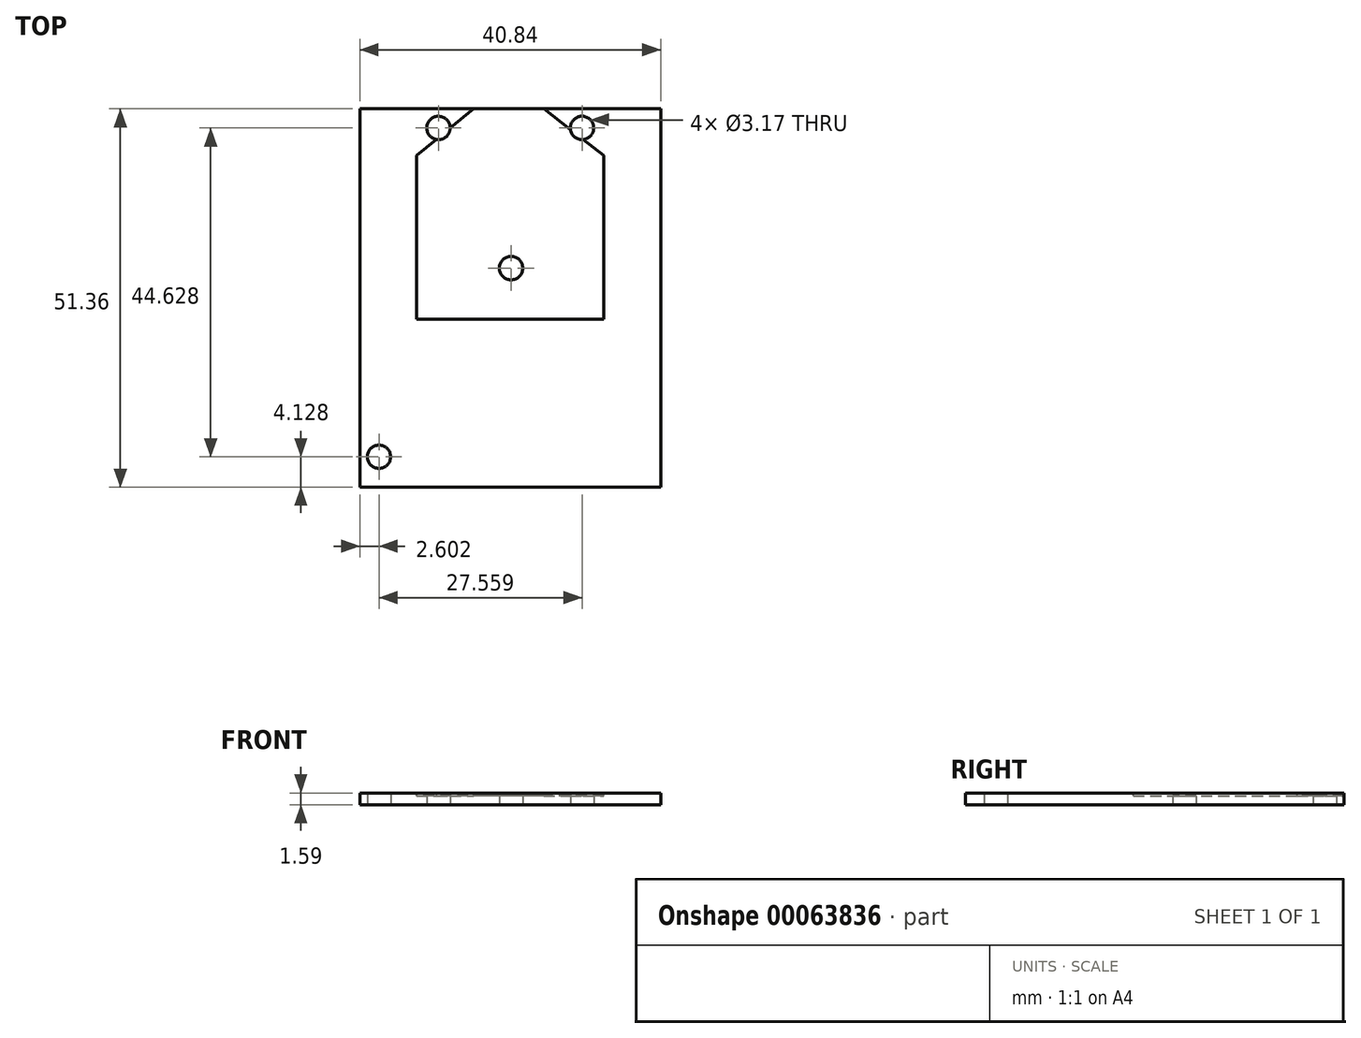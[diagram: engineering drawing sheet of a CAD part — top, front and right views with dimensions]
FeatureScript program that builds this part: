
annotation { "Feature Type Name" : "Feature", "Feature Type Description" : "" }
export const myFeature = defineFeature(function(context is Context, id is Id, definition is map)
    precondition{}
    {
        {
            var Q0;
            Q0=qCreatedBy(makeId("Top.planeOp"),FACE);
            var sketch = newSketch(context, id + "F0", { "sketchPlane" : qUnion([Q0])});
            skLineSegment(sketch, "E0.rect.bottom", {"start": v(20.42, 25.68) * mm, "end": v(-20.42, 25.68) * mm});
            skLineSegment(sketch, "E0.rect.top", {"start": v(20.42, -25.68) * mm, "end": v(-20.42, -25.68) * mm});
            skLineSegment(sketch, "E0.rect.left", {"start": v(20.42, 25.68) * mm, "end": v(20.42, -25.68) * mm});
            skLineSegment(sketch, "E0.rect.right", {"start": v(-20.42, 25.68) * mm, "end": v(-20.42, -25.68) * mm});
            skPoint(sketch, "E0.rect.middle", {"position": v(0, 0) * mm});
            skCircle(sketch, "E1", {"center": v(-9.74, 23.08) * mm, "radius": 1.59 * mm});
            skCircle(sketch, "E2", {"center": v(9.74, 23.08) * mm, "radius": 1.59 * mm});
            skCircle(sketch, "E3", {"center": v(0.11, 4.05) * mm, "radius": 1.59 * mm});
            skCircle(sketch, "E4", {"center": v(-17.82, -21.55) * mm, "radius": 1.59 * mm});
            skPoint(sketch, "E5", {"position": v(0, 18.71) * mm});
            skLineSegment(sketch, "E6", {"start": v(-9.74, 23.08) * mm, "end": v(9.74, 23.08) * mm, "construction": true});
            skPoint(sketch, "E7", {"position": v(0, 23.08) * mm});
            skSolve(sketch);
        }
        {
            var Q0;
            Q0=qSketchRegion(id+"F0",true);
            extrude(context, id + "F1", {"entities" : qUnion([Q0]), "depth" : 1.59 * mm});
        }
        {
            var Q0;
            Q0=makeQuery(id+"F1.opExtrude","CAP_FACE",FACE,{"disambiguationData":[OSD([sQuery(id+"F0.wireOp",EDGE,"E0.rect.bottom"),sQuery(id+"F0.wireOp",EDGE,"E0.rect.top"),sQuery(id+"F0.wireOp",EDGE,"E0.rect.left"),sQuery(id+"F0.wireOp",EDGE,"E0.rect.right"),sQuery(id+"F0.wireOp",EDGE,"E1"),sQuery(id+"F0.wireOp",EDGE,"E2"),sQuery(id+"F0.wireOp",EDGE,"E3"),sQuery(id+"F0.wireOp",EDGE,"E4")])],"isStart":false});
            var sketch = newSketch(context, id + "F2", { "sketchPlane" : qUnion([Q0])});
            skLineSegment(sketch, "E8", {"start": v(-4.98, 25.68) * mm, "end": v(4.55, 25.68) * mm});
            skLineSegment(sketch, "E9", {"start": v(4.55, 25.68) * mm, "end": v(12.7, 19.33) * mm});
            skLineSegment(sketch, "E10", {"start": v(12.7, 19.33) * mm, "end": v(12.7, -2.9) * mm});
            skLineSegment(sketch, "E11", {"start": v(12.7, -2.9) * mm, "end": v(-12.7, -2.9) * mm});
            skLineSegment(sketch, "E12", {"start": v(-12.7, -2.9) * mm, "end": v(-12.7, 19.33) * mm});
            skLineSegment(sketch, "E13", {"start": v(-12.7, 19.33) * mm, "end": v(-4.98, 25.68) * mm});
            skLineSegment(sketch, "E14", {"start": v(-12.7, 19.33) * mm, "end": v(12.7, 19.33) * mm, "construction": true});
            skPoint(sketch, "E15", {"position": v(0, 19.33) * mm});
            skSolve(sketch);
        }
        {
            var Q0;
            Q0=qSketchRegion(id+"F2",true);
            extrude(context, id + "F3", {"entities" : qUnion([Q0]), "operationType" : NewBodyOperationType.REMOVE, "oppositeDirection" : true, "depth" : 0.4 * mm});
        }
    });
